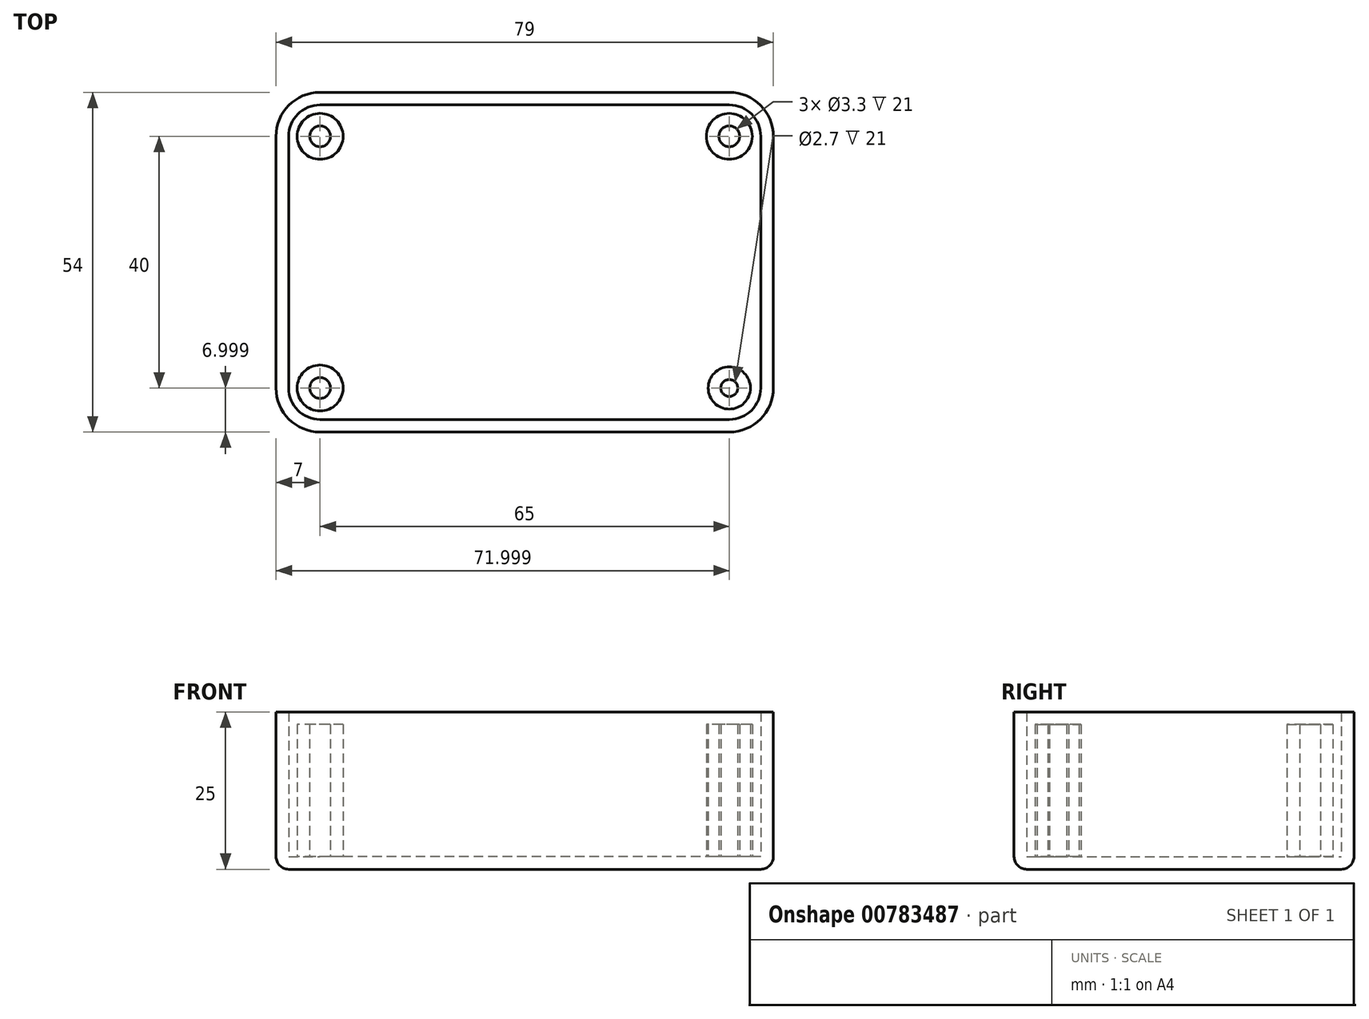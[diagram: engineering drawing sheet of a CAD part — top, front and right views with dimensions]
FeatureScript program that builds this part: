
annotation { "Feature Type Name" : "Feature", "Feature Type Description" : "" }
export const myFeature = defineFeature(function(context is Context, id is Id, definition is map)
    precondition{}
    {
        {
            assignVariable(context, id + "F0", {"name" : "Height", "anyValue" : 25});
        }
        {
            var Q0;
            Q0=qCreatedBy(makeId("Top.planeOp"),FACE);
            var sketch = newSketch(context, id + "F1", { "sketchPlane" : qUnion([Q0])});
            skLineSegment(sketch, "E0.bottom", {"start": v(-22.16, 15.96) * mm, "end": v(42.84, 15.96) * mm});
            skLineSegment(sketch, "E0.top", {"start": v(-22.16, -34.04) * mm, "end": v(42.84, -34.04) * mm});
            skLineSegment(sketch, "E0.left", {"start": v(-27.16, 10.96) * mm, "end": v(-27.16, -29.04) * mm});
            skLineSegment(sketch, "E0.right", {"start": v(47.84, 10.96) * mm, "end": v(47.84, -29.04) * mm});
            skPoint(sketch, "E1.visualSharp", {"position": v(-27.16, 15.96) * mm});
            skArc(sketch, "E1.filletArc", {"start": v(-22.16, 15.96) * mm, "mid": v(-25.7, 14.5) * mm, "end": v(-27.16, 10.96) * mm});
            skPoint(sketch, "E2.visualSharp", {"position": v(47.84, 15.96) * mm});
            skArc(sketch, "E2.filletArc", {"start": v(47.84, 10.96) * mm, "mid": v(46.37, 14.5) * mm, "end": v(42.84, 15.96) * mm});
            skPoint(sketch, "E3.visualSharp", {"position": v(47.84, -34.04) * mm});
            skArc(sketch, "E3.filletArc", {"start": v(42.84, -34.04) * mm, "mid": v(46.37, -32.58) * mm, "end": v(47.84, -29.04) * mm});
            skPoint(sketch, "E4.visualSharp", {"position": v(-27.16, -34.04) * mm});
            skArc(sketch, "E4.filletArc", {"start": v(-27.16, -29.04) * mm, "mid": v(-25.7, -32.58) * mm, "end": v(-22.16, -34.04) * mm});
            skCircle(sketch, "E5", {"center": v(-22.16, -29.04) * mm, "radius": 1.65 * mm});
            skCircle(sketch, "E6", {"center": v(42.84, 10.96) * mm, "radius": 1.65 * mm});
            skCircle(sketch, "E7", {"center": v(42.84, -29.04) * mm, "radius": 1.35 * mm});
            skCircle(sketch, "E8", {"center": v(-22.16, 10.96) * mm, "radius": 1.65 * mm});
            skCircle(sketch, "E9.0", {"center": v(-22.16, -29.04) * mm, "radius": 3.65 * mm});
            skCircle(sketch, "E10.0", {"center": v(-22.16, 10.96) * mm, "radius": 3.65 * mm});
            skCircle(sketch, "E11.0", {"center": v(42.84, 10.96) * mm, "radius": 3.65 * mm});
            skCircle(sketch, "E12.0", {"center": v(42.84, -29.04) * mm, "radius": 3.35 * mm});
            skArc(sketch, "E13.0", {"start": v(-22.16, 17.96) * mm, "mid": v(-27.11, 15.9) * mm, "end": v(-29.16, 10.96) * mm});
            skLineSegment(sketch, "E13.1", {"start": v(-29.16, 10.96) * mm, "end": v(-29.16, -29.04) * mm});
            skLineSegment(sketch, "E13.2", {"start": v(-22.16, 17.96) * mm, "end": v(42.84, 17.96) * mm});
            skArc(sketch, "E13.3", {"start": v(-29.16, -29.04) * mm, "mid": v(-27.11, -34) * mm, "end": v(-22.16, -36.04) * mm});
            skArc(sketch, "E13.4", {"start": v(49.84, 10.96) * mm, "mid": v(47.79, 15.9) * mm, "end": v(42.84, 17.96) * mm});
            skLineSegment(sketch, "E13.5", {"start": v(49.84, 10.96) * mm, "end": v(49.84, -29.04) * mm});
            skArc(sketch, "E13.6", {"start": v(42.84, -36.04) * mm, "mid": v(47.79, -34) * mm, "end": v(49.84, -29.04) * mm});
            skLineSegment(sketch, "E13.7", {"start": v(-22.16, -36.04) * mm, "end": v(42.84, -36.04) * mm});
            skSolve(sketch);
        }
        {
            var Q0;
            Q0=makeQuery(id+"F1.imprint","IMPRINT",FACE,{"disambiguationData":[TD([[makeQuery(id+"F1.imprint","IMPRINT",EDGE,{"derivedFrom":sQuery(id+"F1.wireOp",EDGE,"E0.bottom")}),-1.0]])]});
            var Q1;
            Q1=makeQuery(id+"F1.imprint","IMPRINT",FACE,{"disambiguationData":[TD([[makeQuery(id+"F1.imprint","IMPRINT",EDGE,{"derivedFrom":sQuery(id+"F1.wireOp",EDGE,"E7")}),-1.0]])]});
            var Q2;
            Q2=makeQuery(id+"F1.imprint","IMPRINT",FACE,{"disambiguationData":[TD([[makeQuery(id+"F1.imprint","IMPRINT",EDGE,{"derivedFrom":sQuery(id+"F1.wireOp",EDGE,"E7")}),1.0]])]});
            var Q3;
            Q3=makeQuery(id+"F1.imprint","IMPRINT",FACE,{"disambiguationData":[TD([[makeQuery(id+"F1.imprint","IMPRINT",EDGE,{"derivedFrom":sQuery(id+"F1.wireOp",EDGE,"E6")}),-1.0]])]});
            var Q4;
            Q4=makeQuery(id+"F1.imprint","IMPRINT",FACE,{"disambiguationData":[TD([[makeQuery(id+"F1.imprint","IMPRINT",EDGE,{"derivedFrom":sQuery(id+"F1.wireOp",EDGE,"E6")}),1.0]])]});
            var Q5;
            Q5=makeQuery(id+"F1.imprint","IMPRINT",FACE,{"disambiguationData":[TD([[makeQuery(id+"F1.imprint","IMPRINT",EDGE,{"derivedFrom":sQuery(id+"F1.wireOp",EDGE,"E0.bottom")}),1.0]])]});
            var Q6;
            Q6=makeQuery(id+"F1.imprint","IMPRINT",FACE,{"disambiguationData":[TD([[makeQuery(id+"F1.imprint","IMPRINT",EDGE,{"derivedFrom":sQuery(id+"F1.wireOp",EDGE,"E8")}),-1.0]])]});
            var Q7;
            Q7=makeQuery(id+"F1.imprint","IMPRINT",FACE,{"disambiguationData":[TD([[makeQuery(id+"F1.imprint","IMPRINT",EDGE,{"derivedFrom":sQuery(id+"F1.wireOp",EDGE,"E8")}),1.0]])]});
            var Q8;
            Q8=makeQuery(id+"F1.imprint","IMPRINT",FACE,{"disambiguationData":[TD([[makeQuery(id+"F1.imprint","IMPRINT",EDGE,{"derivedFrom":sQuery(id+"F1.wireOp",EDGE,"E5")}),-1.0]])]});
            var Q9;
            Q9=makeQuery(id+"F1.imprint","IMPRINT",FACE,{"disambiguationData":[TD([[makeQuery(id+"F1.imprint","IMPRINT",EDGE,{"derivedFrom":sQuery(id+"F1.wireOp",EDGE,"E5")}),1.0]])]});
            extrude(context, id + "F2", {"entities" : qUnion([Q0, Q1, Q2, Q3, Q4, Q5, Q6, Q7, Q8, Q9]), "depth" : 2 * mm, "offsetDistance" : 25 * mm});
        }
        {
            var Q0;
            Q0=makeQuery(id+"F1.imprint","IMPRINT",FACE,{"disambiguationData":[TD([[makeQuery(id+"F1.imprint","IMPRINT",EDGE,{"derivedFrom":sQuery(id+"F1.wireOp",EDGE,"E0.bottom")}),1.0]])]});
            extrude(context, id + "F3", {"entities" : qUnion([Q0]), "operationType" : NewBodyOperationType.ADD, "depth" : (getVariable(context, 'Height')) * mm, "offsetDistance" : 25 * mm});
        }
        {
            var Q0;
            Q0=makeQuery(id+"F1.imprint","IMPRINT",FACE,{"disambiguationData":[TD([[makeQuery(id+"F1.imprint","IMPRINT",EDGE,{"derivedFrom":sQuery(id+"F1.wireOp",EDGE,"E6")}),-1.0]])]});
            var Q1;
            Q1=makeQuery(id+"F1.imprint","IMPRINT",FACE,{"disambiguationData":[TD([[makeQuery(id+"F1.imprint","IMPRINT",EDGE,{"derivedFrom":sQuery(id+"F1.wireOp",EDGE,"E7")}),-1.0]])]});
            var Q2;
            Q2=makeQuery(id+"F1.imprint","IMPRINT",FACE,{"disambiguationData":[TD([[makeQuery(id+"F1.imprint","IMPRINT",EDGE,{"derivedFrom":sQuery(id+"F1.wireOp",EDGE,"E8")}),-1.0]])]});
            var Q3;
            Q3=makeQuery(id+"F1.imprint","IMPRINT",FACE,{"disambiguationData":[TD([[makeQuery(id+"F1.imprint","IMPRINT",EDGE,{"derivedFrom":sQuery(id+"F1.wireOp",EDGE,"E5")}),-1.0]])]});
            extrude(context, id + "F4", {"entities" : qUnion([Q0, Q1, Q2, Q3]), "operationType" : NewBodyOperationType.ADD, "depth" : (getVariable(context, 'Height') - 2) * mm, "offsetDistance" : 25 * mm});
        }
        {
            var Q0;
            Q0=makeQuery(id+"F2.opExtrude","CAP_EDGE",EDGE,{"disambiguationData":[OSD([sQuery(id+"F1.wireOp",EDGE,"E13.7")])],"isStart":true});
            fillet(context, id + "F5", {"entities" : qUnion([Q0]), "radius" : 2 * mm, "tangentPropagation" : true, "allowEdgeOverflow" : false});
        }
    });
